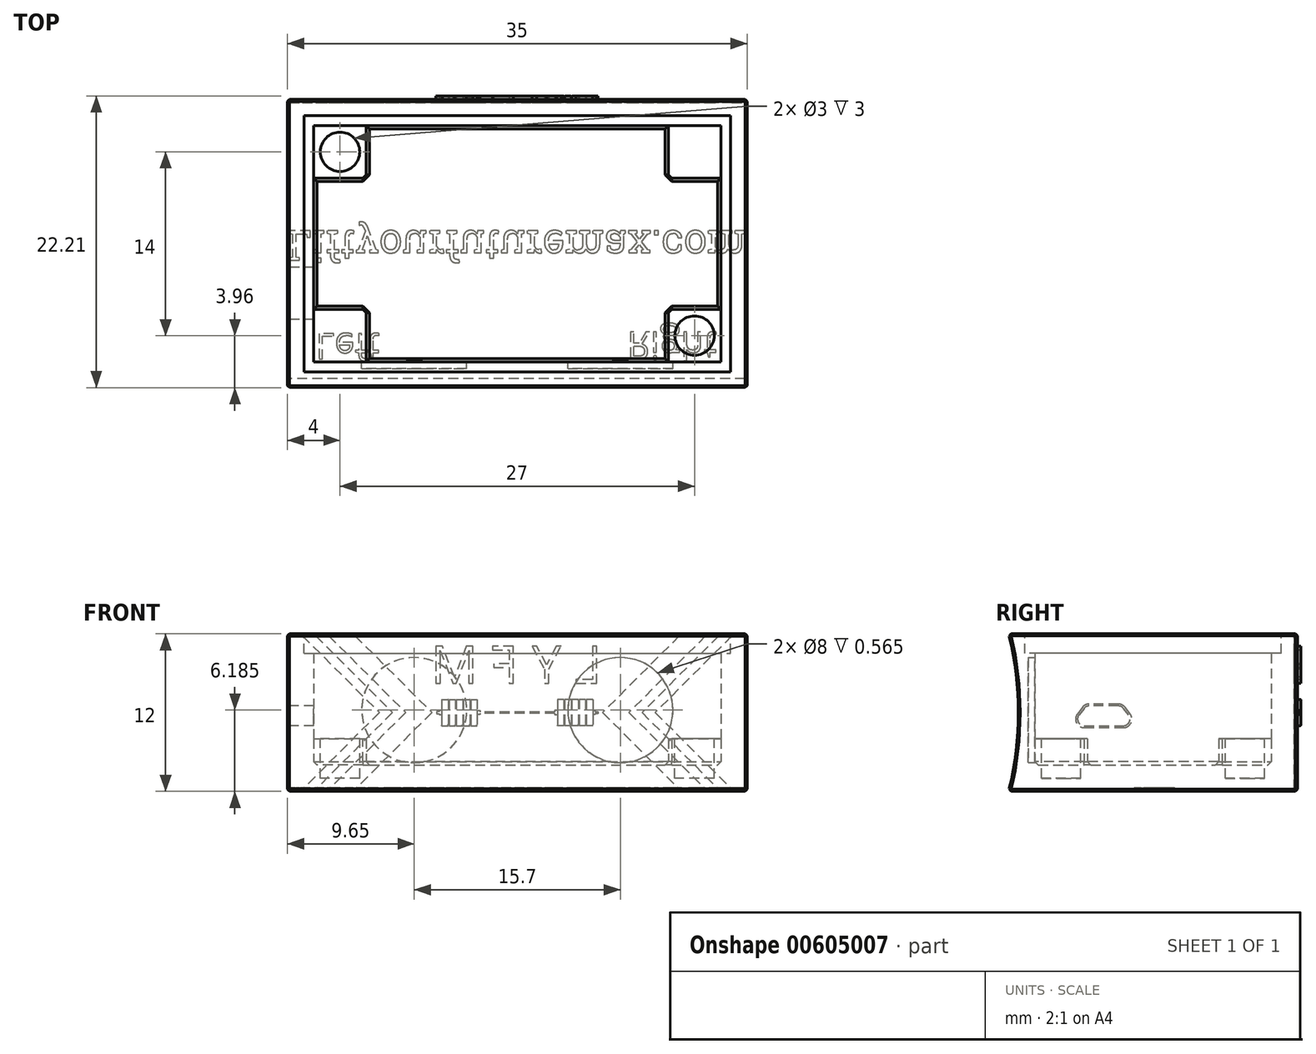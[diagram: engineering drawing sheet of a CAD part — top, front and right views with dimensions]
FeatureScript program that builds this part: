
annotation { "Feature Type Name" : "Feature", "Feature Type Description" : "" }
export const myFeature = defineFeature(function(context is Context, id is Id, definition is map)
    precondition{}
    {
        {
            var Q0;
            Q0=qCreatedBy(makeId("Top.planeOp"),FACE);
            var sketch = newSketch(context, id + "F0", { "sketchPlane" : qUnion([Q0])});
            skLineSegment(sketch, "E0.bottom", {"start": v(-17.5, 11) * mm, "end": v(17.5, 11) * mm});
            skLineSegment(sketch, "E0.top", {"start": v(-17.5, -11) * mm, "end": v(17.5, -11) * mm});
            skLineSegment(sketch, "E0.left", {"start": v(-17.5, 11) * mm, "end": v(-17.5, -11) * mm});
            skLineSegment(sketch, "E0.right", {"start": v(17.5, 11) * mm, "end": v(17.5, -11) * mm});
            skSolve(sketch);
        }
        {
            var Q0;
            Q0=qSketchRegion(id+"F0",true);
            extrude(context, id + "F1", {"entities" : qUnion([Q0]), "depth" : 12 * mm, "offsetDistance" : 25 * mm});
        }
        {
            var Q0;
            Q0=makeQuery(id+"F1.opExtrude","CAP_FACE",FACE,{"disambiguationData":[OSD([sQuery(id+"F0.wireOp",EDGE,"E0.bottom"),sQuery(id+"F0.wireOp",EDGE,"E0.top"),sQuery(id+"F0.wireOp",EDGE,"E0.left"),sQuery(id+"F0.wireOp",EDGE,"E0.right")])],"isStart":false});
            shell(context, id + "F2", {"entities" : qUnion([Q0]), "thickness" : 2 * mm});
        }
        {
            var Q0;
            Q0=makeQuery(id+"F2.opShell","OFFSET_FACE",FACE,{"disambiguationData":[OSD([sQuery(id+"F0.wireOp",EDGE,"E0.bottom"),sQuery(id+"F0.wireOp",EDGE,"E0.top"),sQuery(id+"F0.wireOp",EDGE,"E0.left"),sQuery(id+"F0.wireOp",EDGE,"E0.right")])]});
            var sketch = newSketch(context, id + "F3", { "sketchPlane" : qUnion([Q0])});
            skLineSegment(sketch, "E1.bottom", {"start": v(-15.5, 9) * mm, "end": v(-11.5, 9) * mm});
            skLineSegment(sketch, "E1.top", {"start": v(-15.5, 5) * mm, "end": v(-11.5, 5) * mm});
            skLineSegment(sketch, "E1.left", {"start": v(-15.5, 9) * mm, "end": v(-15.5, 5) * mm});
            skLineSegment(sketch, "E1.right", {"start": v(-11.5, 9) * mm, "end": v(-11.5, 5) * mm});
            skLineSegment(sketch, "E2.bottom", {"start": v(15.5, 9) * mm, "end": v(11.5, 9) * mm});
            skLineSegment(sketch, "E2.top", {"start": v(15.5, 5) * mm, "end": v(11.5, 5) * mm});
            skLineSegment(sketch, "E2.left", {"start": v(15.5, 9) * mm, "end": v(15.5, 5) * mm});
            skLineSegment(sketch, "E2.right", {"start": v(11.5, 9) * mm, "end": v(11.5, 5) * mm});
            skLineSegment(sketch, "E3.bottom", {"start": v(15.5, -9) * mm, "end": v(11.5, -9) * mm});
            skLineSegment(sketch, "E3.top", {"start": v(15.5, -5) * mm, "end": v(11.5, -5) * mm});
            skLineSegment(sketch, "E3.left", {"start": v(15.5, -9) * mm, "end": v(15.5, -5) * mm});
            skLineSegment(sketch, "E3.right", {"start": v(11.5, -9) * mm, "end": v(11.5, -5) * mm});
            skLineSegment(sketch, "E4.bottom", {"start": v(-15.5, -9) * mm, "end": v(-11.5, -9) * mm});
            skLineSegment(sketch, "E4.top", {"start": v(-15.5, -5) * mm, "end": v(-11.5, -5) * mm});
            skLineSegment(sketch, "E4.left", {"start": v(-15.5, -9) * mm, "end": v(-15.5, -5) * mm});
            skLineSegment(sketch, "E4.right", {"start": v(-11.5, -9) * mm, "end": v(-11.5, -5) * mm});
            skSolve(sketch);
        }
        {
            var Q0;
            Q0=qSketchRegion(id+"F3",true);
            extrude(context, id + "F4", {"entities" : qUnion([Q0]), "operationType" : NewBodyOperationType.ADD, "depth" : 2 * mm, "offsetDistance" : 25 * mm});
        }
        {
            var Q0;
            Q0=makeQuery(id+"F4.opExtrude","SWEPT_EDGE",EDGE,{"disambiguationData":[OSD([sQuery(id+"F3.wireOp",EDGE,"E1.top"),sQuery(id+"F3.wireOp",EDGE,"E1.right")])]});
            var Q1;
            {var subQ0=sQuery(id+"F0.wireOp",EDGE,"E0.bottom");Q1=makeQuery(id+"F2.opShell","OFFSET_EDGE",EDGE,{"disambiguationData":[OSD([subQ0]),TDD([makeQuery(id+"F1.opExtrude","CAP_EDGE",EDGE,{"disambiguationData":[OSD([subQ0])],"isStart":true})])]});}
            var Q2;
            {var subQ0=sQuery(id+"F0.wireOp",EDGE,"E0.left");Q2=makeQuery(id+"F2.opShell","OFFSET_EDGE",EDGE,{"disambiguationData":[OSD([subQ0]),TDD([makeQuery(id+"F1.opExtrude","CAP_EDGE",EDGE,{"disambiguationData":[OSD([subQ0])],"isStart":true})])]});}
            var Q3;
            Q3=makeQuery(id+"F2.opShell","OFFSET_FACE",FACE,{"disambiguationData":[OSD([sQuery(id+"F0.wireOp",EDGE,"E0.bottom"),sQuery(id+"F0.wireOp",EDGE,"E0.top"),sQuery(id+"F0.wireOp",EDGE,"E0.left"),sQuery(id+"F0.wireOp",EDGE,"E0.right")])]});
            var Q4;
            Q4=makeQuery(id+"F4.opExtrude","SWEPT_EDGE",EDGE,{"disambiguationData":[OSD([sQuery(id+"F3.wireOp",EDGE,"E2.top"),sQuery(id+"F3.wireOp",EDGE,"E2.right")])]});
            var Q5;
            Q5=makeQuery(id+"F4.opExtrude","SWEPT_EDGE",EDGE,{"disambiguationData":[OSD([sQuery(id+"F3.wireOp",EDGE,"E3.top"),sQuery(id+"F3.wireOp",EDGE,"E3.right")])]});
            var Q6;
            Q6=makeQuery(id+"F4.opExtrude","SWEPT_EDGE",EDGE,{"disambiguationData":[OSD([sQuery(id+"F3.wireOp",EDGE,"E4.top"),sQuery(id+"F3.wireOp",EDGE,"E4.right")])]});
            chamfer(context, id + "F5", {"entities" : qUnion([Q0, Q1, Q2, Q3, Q4, Q5, Q6]), "width" : 0.25 * mm, "tangentPropagation" : true});
        }
        {
            var Q0;
            Q0=makeQuery(id+"F4.opExtrude","CAP_FACE",FACE,{"disambiguationData":[OSD([sQuery(id+"F3.wireOp",EDGE,"E1.bottom"),sQuery(id+"F3.wireOp",EDGE,"E1.top"),sQuery(id+"F3.wireOp",EDGE,"E1.left"),sQuery(id+"F3.wireOp",EDGE,"E1.right")])],"isStart":false});
            var sketch = newSketch(context, id + "F6", { "sketchPlane" : qUnion([Q0])});
            skCircle(sketch, "E5", {"center": v(-13.5, 7) * mm, "radius": 1.5 * mm});
            skPoint(sketch, "E5.centerSnap0", {"position": v(-13.5, 5.88) * mm});
            skPoint(sketch, "E5.centerSnap1", {"position": v(-12.5, 7) * mm});
            skCircle(sketch, "E6.MirrorC", {"center": v(13.5, 7) * mm, "radius": 1.5 * mm});
            skCircle(sketch, "E7.MirrorC", {"center": v(-13.5, -7) * mm, "radius": 1.5 * mm});
            skCircle(sketch, "E8.MirrorC", {"center": v(13.5, -7) * mm, "radius": 1.5 * mm});
            skSolve(sketch);
        }
        {
            var Q0;
            Q0=makeQuery(id+"F6.imprint","IMPRINT",FACE,{"disambiguationData":[TD([[makeQuery(id+"F6.imprint","IMPRINT",EDGE,{"derivedFrom":sQuery(id+"F6.wireOp",EDGE,"E5")}),1.0]])]});
            var Q1;
            Q1=makeQuery(id+"F6.imprint","IMPRINT",FACE,{"disambiguationData":[TD([[makeQuery(id+"F6.imprint","IMPRINT",EDGE,{"derivedFrom":sQuery(id+"F6.wireOp",EDGE,"E6.MirrorC")}),-1.0]])]});
            var Q2;
            Q2=makeQuery(id+"F6.imprint","IMPRINT",FACE,{"disambiguationData":[TD([[makeQuery(id+"F6.imprint","IMPRINT",EDGE,{"derivedFrom":sQuery(id+"F6.wireOp",EDGE,"E8.MirrorC")}),1.0]])]});
            var Q3;
            Q3=makeQuery(id+"F6.imprint","IMPRINT",FACE,{"disambiguationData":[TD([[makeQuery(id+"F6.imprint","IMPRINT",EDGE,{"derivedFrom":sQuery(id+"F6.wireOp",EDGE,"E7.MirrorC")}),-1.0]])]});
            extrude(context, id + "F7", {"entities" : qUnion([Q0, Q1, Q2, Q3]), "operationType" : NewBodyOperationType.REMOVE, "oppositeDirection" : true, "depth" : 3 * mm, "offsetDistance" : 25 * mm});
        }
        {
            var Q0;
            Q0=makeQuery(id+"F1.opExtrude","SWEPT_FACE",FACE,{"disambiguationData":[OSD([sQuery(id+"F0.wireOp",EDGE,"E0.left")])]});
            var sketch = newSketch(context, id + "F8", { "sketchPlane" : qUnion([Q0])});
            skLineSegment(sketch, "E9", {"start": v(1.25, 5) * mm, "end": v(6.25, 5) * mm});
            skLineSegment(sketch, "E10", {"start": v(6.25, 5) * mm, "end": v(5.12, 6.5) * mm});
            skLineSegment(sketch, "E11", {"start": v(5.12, 6.5) * mm, "end": v(2.4, 6.5) * mm});
            skLineSegment(sketch, "E12", {"start": v(2.4, 6.5) * mm, "end": v(1.25, 5) * mm});
            skSolve(sketch);
        }
        {
            var Q0;
            Q0=qSketchRegion(id+"F8",true);
            extrude(context, id + "F9", {"entities" : qUnion([Q0]), "operationType" : NewBodyOperationType.REMOVE, "oppositeDirection" : true, "depth" : 5 * mm, "offsetDistance" : 25 * mm});
        }
        {
            var Q0;
            Q0=makeQuery(id+"F9.boolean.opBoolean","COPY",EDGE,{"derivedFrom":makeQuery(id+"F9.opExtrude","SWEPT_EDGE",EDGE,{"disambiguationData":[OSD([sQuery(id+"F8.wireOp",EDGE,"E9"),sQuery(id+"F8.wireOp",EDGE,"E10")])]})});
            var Q1;
            Q1=makeQuery(id+"F9.boolean.opBoolean","COPY",EDGE,{"derivedFrom":makeQuery(id+"F9.opExtrude","SWEPT_EDGE",EDGE,{"disambiguationData":[OSD([sQuery(id+"F8.wireOp",EDGE,"E9"),sQuery(id+"F8.wireOp",EDGE,"E12")])]})});
            var Q2;
            Q2=makeQuery(id+"F9.boolean.opBoolean","COPY",EDGE,{"derivedFrom":makeQuery(id+"F9.opExtrude","SWEPT_EDGE",EDGE,{"disambiguationData":[OSD([sQuery(id+"F8.wireOp",EDGE,"E10"),sQuery(id+"F8.wireOp",EDGE,"E11")])]})});
            var Q3;
            Q3=makeQuery(id+"F9.boolean.opBoolean","COPY",EDGE,{"derivedFrom":makeQuery(id+"F9.opExtrude","SWEPT_EDGE",EDGE,{"disambiguationData":[OSD([sQuery(id+"F8.wireOp",EDGE,"E11"),sQuery(id+"F8.wireOp",EDGE,"E12")])]})});
            fillet(context, id + "F10", {"entities" : qUnion([Q0, Q1, Q2, Q3]), "radius" : 0.5 * mm, "tangentPropagation" : true, "allowEdgeOverflow" : false});
        }
        {
            var Q0;
            Q0=makeQuery(id+"F1.opExtrude","CAP_FACE",FACE,{"disambiguationData":[OSD([sQuery(id+"F0.wireOp",EDGE,"E0.bottom"),sQuery(id+"F0.wireOp",EDGE,"E0.top"),sQuery(id+"F0.wireOp",EDGE,"E0.left"),sQuery(id+"F0.wireOp",EDGE,"E0.right")])],"isStart":true});
            var sketch = newSketch(context, id + "F11", { "sketchPlane" : qUnion([Q0])});
            skText(sketch, "E13", { "text": "Liftyourfuturemax.com", "fontName": "RobotoSlab-Regular.ttf"});
            const initialGuessF11  = {"E13": [-0.0175, -0.00099, 1, 0, 0.00228]};
            skSetInitialGuess(sketch, initialGuessF11);
            skSolve(sketch);
        }
        {
            var Q0;
            Q0=qSketchRegion(id+"F11",true);
            extrude(context, id + "F12", {"entities" : qUnion([Q0]), "operationType" : NewBodyOperationType.REMOVE, "oppositeDirection" : true, "depth" : 0.25 * mm, "offsetDistance" : 25 * mm});
        }
        {
            var Q0;
            Q0=makeQuery(id+"F1.opExtrude","SWEPT_FACE",FACE,{"disambiguationData":[OSD([sQuery(id+"F0.wireOp",EDGE,"E0.left")])]});
            var sketch = newSketch(context, id + "F13", { "sketchPlane" : qUnion([Q0])});
            skArc(sketch, "E14", {"start": v(11, 12) * mm, "mid": v(10.27, 6) * mm, "end": v(11, 0) * mm});
            skSolve(sketch);
        }
        {
            var Q0;
            Q0=makeQuery(id+"F13.imprint","IMPRINT",FACE,{"disambiguationData":[TD([[makeQuery(id+"F13.imprint","IMPRINT",EDGE,{"derivedFrom":sQuery(id+"F13.wireOp",EDGE,"E14")}),1.0]])]});
            extrude(context, id + "F14", {"entities" : qUnion([Q0]), "operationType" : NewBodyOperationType.REMOVE, "oppositeDirection" : true, "depth" : 50 * mm, "offsetDistance" : 25 * mm});
        }
        {
            var Q0;
            Q0=makeQuery(id+"F1.opExtrude","SWEPT_FACE",FACE,{"disambiguationData":[OSD([sQuery(id+"F0.wireOp",EDGE,"E0.right")])]});
            var Q1;
            Q1=makeQuery(id+"F1.opExtrude","SWEPT_FACE",FACE,{"disambiguationData":[OSD([sQuery(id+"F0.wireOp",EDGE,"E0.bottom")])]});
            var Q2;
            Q2=makeQuery(id+"F1.opExtrude","SWEPT_FACE",FACE,{"disambiguationData":[OSD([sQuery(id+"F0.wireOp",EDGE,"E0.left")])]});
            var Q3;
            Q3=makeQuery(id+"F14.boolean.opBoolean","COPY",FACE,{"derivedFrom":makeQuery(id+"F14.opExtrude","SWEPT_FACE",FACE,{"disambiguationData":[OSD([sQuery(id+"F13.wireOp",EDGE,"E14")])]})});
            chamfer(context, id + "F15", {"entities" : qUnion([Q0, Q1, Q2, Q3]), "width" : 0.15 * mm, "tangentPropagation" : true});
        }
        {
            var Q0;
            Q0=qCreatedBy(makeId("Front.planeOp"),FACE);
            var sketch = newSketch(context, id + "F16", { "sketchPlane" : qUnion([Q0])});
            skCircle(sketch, "E15", {"center": v(7.85, 6.18) * mm, "radius": 4 * mm});
            skCircle(sketch, "E16", {"center": v(-7.85, 6.18) * mm, "radius": 4 * mm});
            skSolve(sketch);
        }
        {
            var Q0;
            Q0=qSketchRegion(id+"F16",true);
            extrude(context, id + "F17", {"entities" : qUnion([Q0]), "operationType" : NewBodyOperationType.REMOVE, "depth" : 9.5 * mm, "offsetDistance" : 25 * mm});
        }
        {
            var Q0;
            {var subQ0=sQuery(id+"F0.wireOp",EDGE,"E0.right");var subQ1=sQuery(id+"F0.wireOp",EDGE,"E0.left");var subQ2=sQuery(id+"F0.wireOp",EDGE,"E0.top");var subQ3=sQuery(id+"F0.wireOp",EDGE,"E0.bottom");Q0=makeQuery(id+"F12.boolean.opBoolean","SPLIT",FACE,{"disambiguationData":[TD([makeQuery(id+"F1.opExtrude","SWEPT_FACE",FACE,{"disambiguationData":[OSD([subQ3])]})])],"derivedFrom":makeQuery(id+"F1.opExtrude","CAP_FACE",FACE,{"disambiguationData":[OSD([subQ3,subQ2,subQ1,subQ0])],"isStart":true})});}
            var sketch = newSketch(context, id + "F18", { "sketchPlane" : qUnion([Q0])});
            skText(sketch, "E17", { "text": "Left", "fontName": "OpenSans-Regular.ttf"});
            skText(sketch, "E18", { "text": "Right", "fontName": "OpenSans-Regular.ttf"});
            const initialGuessF18  = {"E17": [-0.01535, 0.00683, 1, 0, 0.00198], "E18": [0.00835, 0.00673, 1, 0, 0.00207]};
            skSetInitialGuess(sketch, initialGuessF18);
            skSolve(sketch);
        }
        {
            var Q0;
            Q0=qSketchRegion(id+"F18",true);
            extrude(context, id + "F19", {"entities" : qUnion([Q0]), "operationType" : NewBodyOperationType.REMOVE, "oppositeDirection" : true, "depth" : 0.15 * mm, "offsetDistance" : 25 * mm});
        }
        {
            var Q0;
            Q0=makeQuery(id+"F1.opExtrude","CAP_FACE",FACE,{"disambiguationData":[OSD([sQuery(id+"F0.wireOp",EDGE,"E0.bottom"),sQuery(id+"F0.wireOp",EDGE,"E0.top"),sQuery(id+"F0.wireOp",EDGE,"E0.left"),sQuery(id+"F0.wireOp",EDGE,"E0.right")])],"isStart":false});
            var sketch = newSketch(context, id + "F20", { "sketchPlane" : qUnion([Q0])});
            skLineSegment(sketch, "E19.bottom", {"start": v(-16.25, 9.75) * mm, "end": v(16.25, 9.75) * mm});
            skLineSegment(sketch, "E19.top", {"start": v(-16.25, -9.75) * mm, "end": v(16.25, -9.75) * mm});
            skLineSegment(sketch, "E19.left", {"start": v(-16.25, 9.75) * mm, "end": v(-16.25, -9.75) * mm});
            skLineSegment(sketch, "E19.right", {"start": v(16.25, 9.75) * mm, "end": v(16.25, -9.75) * mm});
            skSolve(sketch);
        }
        {
            var Q0;
            Q0=qSketchRegion(id+"F20",true);
            extrude(context, id + "F21", {"entities" : qUnion([Q0]), "operationType" : NewBodyOperationType.REMOVE, "oppositeDirection" : true, "depth" : 1.5 * mm, "offsetDistance" : 25 * mm});
        }
        {
            var Q0;
            Q0=makeQuery(id+"F1.opExtrude","SWEPT_FACE",FACE,{"disambiguationData":[OSD([sQuery(id+"F0.wireOp",EDGE,"E0.bottom")])]});
            var sketch = newSketch(context, id + "F22", { "sketchPlane" : qUnion([Q0])});
            skLineSegment(sketch, "E20", {"start": v(-16.35, 11.85) * mm, "end": v(-10.5, 6) * mm});
            skLineSegment(sketch, "E21", {"start": v(-10.5, 6) * mm, "end": v(-16.35, 0.15) * mm});
            skLineSegment(sketch, "E22", {"start": v(-15.35, 11.85) * mm, "end": v(-9.5, 6) * mm});
            skPoint(sketch, "E22.endSnap0", {"position": v(-17.35, 6) * mm});
            skLineSegment(sketch, "E23", {"start": v(-9.5, 6) * mm, "end": v(-15.35, 0.15) * mm});
            skLineSegment(sketch, "E24", {"start": v(-14.35, 11.85) * mm, "end": v(-8.5, 6) * mm});
            skLineSegment(sketch, "E25", {"start": v(-8.5, 6) * mm, "end": v(-14.35, 0.15) * mm});
            skLineSegment(sketch, "E26", {"start": v(-13.35, 11.85) * mm, "end": v(-7.5, 6) * mm});
            skLineSegment(sketch, "E27", {"start": v(-7.5, 6) * mm, "end": v(-13.35, 0.15) * mm});
            skLineSegment(sketch, "E28", {"start": v(-12.35, 11.85) * mm, "end": v(-6.5, 6) * mm});
            skLineSegment(sketch, "E29", {"start": v(-6.5, 6) * mm, "end": v(-12.35, 0.15) * mm});
            skLineSegment(sketch, "E30.MirrorCS", {"start": v(12.35, 11.85) * mm, "end": v(6.5, 6) * mm});
            skLineSegment(sketch, "E31.MirrorCS", {"start": v(13.35, 11.85) * mm, "end": v(7.5, 6) * mm});
            skLineSegment(sketch, "E32.MirrorCS", {"start": v(14.35, 11.85) * mm, "end": v(8.5, 6) * mm});
            skLineSegment(sketch, "E33.MirrorCS", {"start": v(15.35, 11.85) * mm, "end": v(9.5, 6) * mm});
            skLineSegment(sketch, "E34.MirrorCS", {"start": v(16.35, 11.85) * mm, "end": v(10.5, 6) * mm});
            skLineSegment(sketch, "E35.MirrorCS", {"start": v(6.5, 6) * mm, "end": v(12.35, 0.15) * mm});
            skLineSegment(sketch, "E36.MirrorCS", {"start": v(7.5, 6) * mm, "end": v(13.35, 0.15) * mm});
            skLineSegment(sketch, "E37.MirrorCS", {"start": v(8.5, 6) * mm, "end": v(14.35, 0.15) * mm});
            skLineSegment(sketch, "E38.MirrorCS", {"start": v(9.5, 6) * mm, "end": v(15.35, 0.15) * mm});
            skLineSegment(sketch, "E39.MirrorCS", {"start": v(10.5, 6) * mm, "end": v(16.35, 0.15) * mm});
            skSolve(sketch);
        }
        {
            var Q0;
            {var subQ3=sQuery(id+"F22.wireOp",EDGE,"E28");Q0=makeQuery(id+"F22.imprint","IMPRINT",FACE,{"disambiguationData":[TD([[makeQuery(id+"F22.imprint","IMPRINT",EDGE,{"derivedFrom":subQ3}),1.0]])]});}
            var Q1;
            {var subQ6=sQuery(id+"F22.wireOp",EDGE,"E20");Q1=makeQuery(id+"F22.imprint","IMPRINT",FACE,{"disambiguationData":[TD([[makeQuery(id+"F22.imprint","IMPRINT",EDGE,{"derivedFrom":subQ6}),-1.0]])]});}
            var Q2;
            {var subQ6=sQuery(id+"F22.wireOp",EDGE,"E34.MirrorCS");Q2=makeQuery(id+"F22.imprint","IMPRINT",FACE,{"disambiguationData":[TD([[makeQuery(id+"F22.imprint","IMPRINT",EDGE,{"derivedFrom":subQ6}),1.0]])]});}
            var Q3;
            {var subQ3=sQuery(id+"F22.wireOp",EDGE,"E22");Q3=makeQuery(id+"F22.imprint","IMPRINT",FACE,{"disambiguationData":[TD([[makeQuery(id+"F22.imprint","IMPRINT",EDGE,{"derivedFrom":subQ3}),1.0]])]});}
            var Q4;
            {var subQ3=sQuery(id+"F22.wireOp",EDGE,"E32.MirrorCS");Q4=makeQuery(id+"F22.imprint","IMPRINT",FACE,{"disambiguationData":[TD([[makeQuery(id+"F22.imprint","IMPRINT",EDGE,{"derivedFrom":subQ3}),1.0]])]});}
            extrude(context, id + "F23", {"entities" : qUnion([Q0, Q1, Q2, Q3, Q4]), "operationType" : NewBodyOperationType.REMOVE, "oppositeDirection" : true, "depth" : 0.25 * mm, "offsetDistance" : 25 * mm});
        }
        {
            var Q0;
            Q0=makeQuery(id+"F23.boolean.opBoolean","COPY",FACE,{"derivedFrom":makeQuery(id+"F23.opExtrude","CAP_FACE",FACE,{"disambiguationData":[OSD([sQuery(id+"F0.wireOp",EDGE,"E0.bottom"),sQuery(id+"F22.wireOp",EDGE,"E28"),sQuery(id+"F22.wireOp",EDGE,"E29"),sQuery(id+"F22.wireOp",EDGE,"E30.MirrorCS"),sQuery(id+"F22.wireOp",EDGE,"E35.MirrorCS")])],"isStart":false})});
            var sketch = newSketch(context, id + "F24", { "sketchPlane" : qUnion([Q0])});
            skLineSegment(sketch, "E40.bottom", {"start": v(-5.2, 7) * mm, "end": v(-4.7, 7) * mm});
            skLineSegment(sketch, "E40.top", {"start": v(-5.2, 5) * mm, "end": v(-4.7, 5) * mm});
            skLineSegment(sketch, "E40.left", {"start": v(-5.2, 7) * mm, "end": v(-5.2, 5) * mm});
            skLineSegment(sketch, "E40.right", {"start": v(-4.7, 7) * mm, "end": v(-4.7, 5) * mm});
            skLineSegment(sketch, "E41.bottom", {"start": v(-4.65, 7) * mm, "end": v(-4.15, 7) * mm});
            skLineSegment(sketch, "E41.top", {"start": v(-4.65, 5) * mm, "end": v(-4.15, 5) * mm});
            skLineSegment(sketch, "E41.left", {"start": v(-4.65, 7) * mm, "end": v(-4.65, 5) * mm});
            skLineSegment(sketch, "E41.right", {"start": v(-4.15, 7) * mm, "end": v(-4.15, 5) * mm});
            skLineSegment(sketch, "E42.bottom", {"start": v(-4.1, 7) * mm, "end": v(-3.6, 7) * mm});
            skLineSegment(sketch, "E42.top", {"start": v(-4.1, 5) * mm, "end": v(-3.6, 5) * mm});
            skLineSegment(sketch, "E42.left", {"start": v(-4.1, 7) * mm, "end": v(-4.1, 5) * mm});
            skLineSegment(sketch, "E42.right", {"start": v(-3.6, 7) * mm, "end": v(-3.6, 5) * mm});
            skLineSegment(sketch, "E43.bottom", {"start": v(-3.55, 7) * mm, "end": v(-3.05, 7) * mm});
            skLineSegment(sketch, "E43.top", {"start": v(-3.55, 5) * mm, "end": v(-3.05, 5) * mm});
            skLineSegment(sketch, "E43.left", {"start": v(-3.55, 7) * mm, "end": v(-3.55, 5) * mm});
            skLineSegment(sketch, "E43.right", {"start": v(-3.05, 7) * mm, "end": v(-3.05, 5) * mm});
            skLineSegment(sketch, "E44.bottom", {"start": v(-5.75, 7) * mm, "end": v(-5.25, 7) * mm});
            skLineSegment(sketch, "E44.top", {"start": v(-5.75, 5) * mm, "end": v(-5.25, 5) * mm});
            skLineSegment(sketch, "E44.left", {"start": v(-5.75, 7) * mm, "end": v(-5.75, 5) * mm});
            skLineSegment(sketch, "E44.right", {"start": v(-5.25, 7) * mm, "end": v(-5.25, 5) * mm});
            skLineSegment(sketch, "E45.MirrorCS", {"start": v(3.05, 7) * mm, "end": v(3.05, 5) * mm});
            skLineSegment(sketch, "E46.MirrorCS", {"start": v(3.55, 7) * mm, "end": v(3.55, 5) * mm});
            skLineSegment(sketch, "E47.MirrorCS", {"start": v(3.6, 7) * mm, "end": v(3.6, 5) * mm});
            skLineSegment(sketch, "E48.MirrorCS", {"start": v(4.1, 7) * mm, "end": v(4.1, 5) * mm});
            skLineSegment(sketch, "E49.MirrorCS", {"start": v(4.15, 7) * mm, "end": v(4.15, 5) * mm});
            skLineSegment(sketch, "E50.MirrorCS", {"start": v(4.65, 7) * mm, "end": v(4.65, 5) * mm});
            skLineSegment(sketch, "E51.MirrorCS", {"start": v(4.7, 7) * mm, "end": v(4.7, 5) * mm});
            skLineSegment(sketch, "E52.MirrorCS", {"start": v(5.2, 7) * mm, "end": v(5.2, 5) * mm});
            skLineSegment(sketch, "E53.MirrorCS", {"start": v(5.25, 7) * mm, "end": v(5.25, 5) * mm});
            skLineSegment(sketch, "E54.MirrorCS", {"start": v(5.75, 7) * mm, "end": v(5.75, 5) * mm});
            skLineSegment(sketch, "E55.MirrorCS", {"start": v(5.75, 7) * mm, "end": v(5.25, 7) * mm});
            skLineSegment(sketch, "E56.MirrorCS", {"start": v(5.2, 7) * mm, "end": v(4.7, 7) * mm});
            skLineSegment(sketch, "E57.MirrorCS", {"start": v(4.65, 7) * mm, "end": v(4.15, 7) * mm});
            skLineSegment(sketch, "E58.MirrorCS", {"start": v(4.1, 7) * mm, "end": v(3.6, 7) * mm});
            skLineSegment(sketch, "E59.MirrorCS", {"start": v(3.55, 7) * mm, "end": v(3.05, 7) * mm});
            skLineSegment(sketch, "E60.MirrorCS", {"start": v(3.55, 5) * mm, "end": v(3.05, 5) * mm});
            skLineSegment(sketch, "E61.MirrorCS", {"start": v(4.1, 5) * mm, "end": v(3.6, 5) * mm});
            skLineSegment(sketch, "E62.MirrorCS", {"start": v(4.65, 5) * mm, "end": v(4.15, 5) * mm});
            skLineSegment(sketch, "E63.MirrorCS", {"start": v(5.2, 5) * mm, "end": v(4.7, 5) * mm});
            skLineSegment(sketch, "E64.MirrorCS", {"start": v(5.75, 5) * mm, "end": v(5.25, 5) * mm});
            skLineSegment(sketch, "E65", {"start": v(-3.05, 6.15) * mm, "end": v(-2.85, 6.15) * mm});
            skLineSegment(sketch, "E66", {"start": v(-2.85, 6.15) * mm, "end": v(-2.85, 5.85) * mm});
            skLineSegment(sketch, "E67", {"start": v(-2.85, 5.85) * mm, "end": v(-3.05, 5.85) * mm});
            skLineSegment(sketch, "E68.MirrorCS", {"start": v(3.05, 6.15) * mm, "end": v(2.85, 6.15) * mm});
            skLineSegment(sketch, "E69.MirrorCS", {"start": v(2.85, 6.15) * mm, "end": v(2.85, 5.85) * mm});
            skLineSegment(sketch, "E70.MirrorCS", {"start": v(2.85, 5.85) * mm, "end": v(3.05, 5.85) * mm});
            skLineSegment(sketch, "E71", {"start": v(-2.85, 6.05) * mm, "end": v(2.85, 6.05) * mm});
            skLineSegment(sketch, "E72", {"start": v(-2.85, 5.95) * mm, "end": v(2.85, 5.95) * mm});
            skLineSegment(sketch, "E73", {"start": v(-5.75, 6.15) * mm, "end": v(-5.94, 6.15) * mm});
            skLineSegment(sketch, "E74", {"start": v(-5.94, 6.15) * mm, "end": v(-5.94, 6.08) * mm});
            skLineSegment(sketch, "E75", {"start": v(-5.94, 6.08) * mm, "end": v(-6.14, 6.08) * mm});
            skLineSegment(sketch, "E76", {"start": v(-6.14, 6.08) * mm, "end": v(-6.14, 5.93) * mm});
            skLineSegment(sketch, "E77", {"start": v(-6.14, 5.93) * mm, "end": v(-5.94, 5.93) * mm});
            skLineSegment(sketch, "E78", {"start": v(-5.94, 5.93) * mm, "end": v(-5.94, 5.85) * mm});
            skLineSegment(sketch, "E79", {"start": v(-5.94, 5.85) * mm, "end": v(-5.75, 5.85) * mm});
            skLineSegment(sketch, "E80.MirrorCS", {"start": v(5.75, 6.15) * mm, "end": v(5.94, 6.15) * mm});
            skLineSegment(sketch, "E81.MirrorCS", {"start": v(5.94, 6.15) * mm, "end": v(5.94, 6.08) * mm});
            skLineSegment(sketch, "E82.MirrorCS", {"start": v(5.94, 6.08) * mm, "end": v(6.14, 6.08) * mm});
            skLineSegment(sketch, "E83.MirrorCS", {"start": v(6.14, 6.08) * mm, "end": v(6.14, 5.93) * mm});
            skLineSegment(sketch, "E84.MirrorCS", {"start": v(6.14, 5.93) * mm, "end": v(5.94, 5.93) * mm});
            skLineSegment(sketch, "E85.MirrorCS", {"start": v(5.94, 5.93) * mm, "end": v(5.94, 5.85) * mm});
            skLineSegment(sketch, "E86.MirrorCS", {"start": v(5.94, 5.85) * mm, "end": v(5.75, 5.85) * mm});
            skSolve(sketch);
        }
        {
            var Q0;
            {var subQ0=sQuery(id+"F24.wireOp",EDGE,"E71");Q0=makeQuery(id+"F24.imprint","IMPRINT",FACE,{"disambiguationData":[TD([[makeQuery(id+"F24.imprint","IMPRINT",EDGE,{"derivedFrom":subQ0}),-1.0]])]});}
            var Q1;
            {var subQ3=sQuery(id+"F24.wireOp",EDGE,"E65");Q1=makeQuery(id+"F24.imprint","IMPRINT",FACE,{"disambiguationData":[TD([[makeQuery(id+"F24.imprint","IMPRINT",EDGE,{"derivedFrom":subQ3}),-1.0]])]});}
            var Q2;
            {var subQ1=sQuery(id+"F24.wireOp",EDGE,"E68.MirrorCS");Q2=makeQuery(id+"F24.imprint","IMPRINT",FACE,{"disambiguationData":[TD([[makeQuery(id+"F24.imprint","IMPRINT",EDGE,{"derivedFrom":subQ1}),1.0]])]});}
            var Q3;
            {var subQ0=sQuery(id+"F24.wireOp",EDGE,"E80.MirrorCS");Q3=makeQuery(id+"F24.imprint","IMPRINT",FACE,{"disambiguationData":[TD([[makeQuery(id+"F24.imprint","IMPRINT",EDGE,{"derivedFrom":subQ0}),-1.0]])]});}
            var Q4;
            {var subQ0=sQuery(id+"F24.wireOp",EDGE,"E73");Q4=makeQuery(id+"F24.imprint","IMPRINT",FACE,{"disambiguationData":[TD([[makeQuery(id+"F24.imprint","IMPRINT",EDGE,{"derivedFrom":subQ0}),1.0]])]});}
            extrude(context, id + "F25", {"entities" : qUnion([Q0, Q1, Q2, Q3, Q4]), "depth" : 0.5 * mm, "offsetDistance" : 25 * mm});
        }
        {
            var Q0;
            Q0=makeQuery(id+"F24.imprint","IMPRINT",FACE,{"disambiguationData":[TD([[makeQuery(id+"F24.imprint","IMPRINT",EDGE,{"derivedFrom":sQuery(id+"F24.wireOp",EDGE,"E53.MirrorCS")}),1.0]])]});
            var Q1;
            Q1=makeQuery(id+"F24.imprint","IMPRINT",FACE,{"disambiguationData":[TD([[makeQuery(id+"F24.imprint","IMPRINT",EDGE,{"derivedFrom":sQuery(id+"F24.wireOp",EDGE,"E51.MirrorCS")}),1.0]])]});
            var Q2;
            Q2=makeQuery(id+"F24.imprint","IMPRINT",FACE,{"disambiguationData":[TD([[makeQuery(id+"F24.imprint","IMPRINT",EDGE,{"derivedFrom":sQuery(id+"F24.wireOp",EDGE,"E49.MirrorCS")}),1.0]])]});
            var Q3;
            Q3=makeQuery(id+"F24.imprint","IMPRINT",FACE,{"disambiguationData":[TD([[makeQuery(id+"F24.imprint","IMPRINT",EDGE,{"derivedFrom":sQuery(id+"F24.wireOp",EDGE,"E47.MirrorCS")}),1.0]])]});
            var Q4;
            Q4=makeQuery(id+"F24.imprint","IMPRINT",FACE,{"disambiguationData":[TD([[makeQuery(id+"F24.imprint","IMPRINT",EDGE,{"derivedFrom":sQuery(id+"F24.wireOp",EDGE,"E46.MirrorCS")}),-1.0]])]});
            var Q5;
            {var subQ3=sQuery(id+"F24.wireOp",EDGE,"E44.bottom");Q5=makeQuery(id+"F24.imprint","IMPRINT",FACE,{"disambiguationData":[TD([[makeQuery(id+"F24.imprint","IMPRINT",EDGE,{"derivedFrom":subQ3}),-1.0]])]});}
            var Q6;
            Q6=makeQuery(id+"F24.imprint","IMPRINT",FACE,{"disambiguationData":[TD([[makeQuery(id+"F24.imprint","IMPRINT",EDGE,{"derivedFrom":sQuery(id+"F24.wireOp",EDGE,"E40.bottom")}),-1.0]])]});
            var Q7;
            Q7=makeQuery(id+"F24.imprint","IMPRINT",FACE,{"disambiguationData":[TD([[makeQuery(id+"F24.imprint","IMPRINT",EDGE,{"derivedFrom":sQuery(id+"F24.wireOp",EDGE,"E41.bottom")}),-1.0]])]});
            var Q8;
            Q8=makeQuery(id+"F24.imprint","IMPRINT",FACE,{"disambiguationData":[TD([[makeQuery(id+"F24.imprint","IMPRINT",EDGE,{"derivedFrom":sQuery(id+"F24.wireOp",EDGE,"E42.bottom")}),-1.0]])]});
            var Q9;
            {var subQ1=sQuery(id+"F24.wireOp",EDGE,"E43.bottom");Q9=makeQuery(id+"F24.imprint","IMPRINT",FACE,{"disambiguationData":[TD([[makeQuery(id+"F24.imprint","IMPRINT",EDGE,{"derivedFrom":subQ1}),-1.0]])]});}
            extrude(context, id + "F26", {"entities" : qUnion([Q0, Q1, Q2, Q3, Q4, Q5, Q6, Q7, Q8, Q9]), "depth" : 0.5 * mm, "offsetDistance" : 25 * mm});
        }
        {
            var Q0;
            Q0=makeQuery(id+"F26.opExtrude","CAP_FACE",FACE,{"disambiguationData":[OSD([sQuery(id+"F24.wireOp",EDGE,"E44.bottom"),sQuery(id+"F24.wireOp",EDGE,"E44.top"),sQuery(id+"F24.wireOp",EDGE,"E44.left"),sQuery(id+"F24.wireOp",EDGE,"E44.right")])],"isStart":false});
            var Q1;
            Q1=makeQuery(id+"F26.opExtrude","CAP_FACE",FACE,{"disambiguationData":[OSD([sQuery(id+"F24.wireOp",EDGE,"E40.bottom"),sQuery(id+"F24.wireOp",EDGE,"E40.top"),sQuery(id+"F24.wireOp",EDGE,"E40.left"),sQuery(id+"F24.wireOp",EDGE,"E40.right")])],"isStart":false});
            var Q2;
            Q2=makeQuery(id+"F26.opExtrude","CAP_FACE",FACE,{"disambiguationData":[OSD([sQuery(id+"F24.wireOp",EDGE,"E41.bottom"),sQuery(id+"F24.wireOp",EDGE,"E41.top"),sQuery(id+"F24.wireOp",EDGE,"E41.left"),sQuery(id+"F24.wireOp",EDGE,"E41.right")])],"isStart":false});
            var Q3;
            Q3=makeQuery(id+"F26.opExtrude","CAP_FACE",FACE,{"disambiguationData":[OSD([sQuery(id+"F24.wireOp",EDGE,"E42.bottom"),sQuery(id+"F24.wireOp",EDGE,"E42.top"),sQuery(id+"F24.wireOp",EDGE,"E42.left"),sQuery(id+"F24.wireOp",EDGE,"E42.right")])],"isStart":false});
            var Q4;
            Q4=makeQuery(id+"F26.opExtrude","CAP_FACE",FACE,{"disambiguationData":[OSD([sQuery(id+"F24.wireOp",EDGE,"E43.bottom"),sQuery(id+"F24.wireOp",EDGE,"E43.top"),sQuery(id+"F24.wireOp",EDGE,"E43.left"),sQuery(id+"F24.wireOp",EDGE,"E43.right")])],"isStart":false});
            var Q5;
            Q5=makeQuery(id+"F26.opExtrude","CAP_FACE",FACE,{"disambiguationData":[OSD([sQuery(id+"F24.wireOp",EDGE,"E45.MirrorCS"),sQuery(id+"F24.wireOp",EDGE,"E46.MirrorCS"),sQuery(id+"F24.wireOp",EDGE,"E59.MirrorCS"),sQuery(id+"F24.wireOp",EDGE,"E60.MirrorCS")])],"isStart":false});
            var Q6;
            Q6=makeQuery(id+"F26.opExtrude","CAP_FACE",FACE,{"disambiguationData":[OSD([sQuery(id+"F24.wireOp",EDGE,"E47.MirrorCS"),sQuery(id+"F24.wireOp",EDGE,"E48.MirrorCS"),sQuery(id+"F24.wireOp",EDGE,"E58.MirrorCS"),sQuery(id+"F24.wireOp",EDGE,"E61.MirrorCS")])],"isStart":false});
            var Q7;
            Q7=makeQuery(id+"F26.opExtrude","CAP_FACE",FACE,{"disambiguationData":[OSD([sQuery(id+"F24.wireOp",EDGE,"E49.MirrorCS"),sQuery(id+"F24.wireOp",EDGE,"E50.MirrorCS"),sQuery(id+"F24.wireOp",EDGE,"E57.MirrorCS"),sQuery(id+"F24.wireOp",EDGE,"E62.MirrorCS")])],"isStart":false});
            var Q8;
            Q8=makeQuery(id+"F26.opExtrude","CAP_FACE",FACE,{"disambiguationData":[OSD([sQuery(id+"F24.wireOp",EDGE,"E51.MirrorCS"),sQuery(id+"F24.wireOp",EDGE,"E52.MirrorCS"),sQuery(id+"F24.wireOp",EDGE,"E56.MirrorCS"),sQuery(id+"F24.wireOp",EDGE,"E63.MirrorCS")])],"isStart":false});
            var Q9;
            Q9=makeQuery(id+"F26.opExtrude","CAP_FACE",FACE,{"disambiguationData":[OSD([sQuery(id+"F24.wireOp",EDGE,"E53.MirrorCS"),sQuery(id+"F24.wireOp",EDGE,"E54.MirrorCS"),sQuery(id+"F24.wireOp",EDGE,"E55.MirrorCS"),sQuery(id+"F24.wireOp",EDGE,"E64.MirrorCS")])],"isStart":false});
            fillet(context, id + "F27", {"entities" : qUnion([Q0, Q1, Q2, Q3, Q4, Q5, Q6, Q7, Q8, Q9]), "radius" : 0.05 * mm, "tangentPropagation" : true, "allowEdgeOverflow" : false});
        }
        {
            var Q0;
            Q0=makeQuery(id+"F23.boolean.opBoolean","COPY",FACE,{"derivedFrom":makeQuery(id+"F23.opExtrude","CAP_FACE",FACE,{"disambiguationData":[OSD([sQuery(id+"F0.wireOp",EDGE,"E0.bottom"),sQuery(id+"F22.wireOp",EDGE,"E28"),sQuery(id+"F22.wireOp",EDGE,"E29"),sQuery(id+"F22.wireOp",EDGE,"E30.MirrorCS"),sQuery(id+"F22.wireOp",EDGE,"E35.MirrorCS")])],"isStart":false})});
            var sketch = newSketch(context, id + "F28", { "sketchPlane" : qUnion([Q0])});
            skText(sketch, "E87", { "text": "L Y F M", "fontName": "OpenSans-Regular.ttf"});
            const initialGuessF28  = {"E87": [-0.00644, 0.00822, 1, 0, 0.00286]};
            skSetInitialGuess(sketch, initialGuessF28);
            skSolve(sketch);
        }
        {
            var Q0;
            Q0 = qSketchRegion(id + "F28", true);
            extrude(context, id + "F29", {"entities" : qUnion([Q0]), "depth" : 0.5 * mm, "offsetDistance" : 25 * mm});
        }
    });
